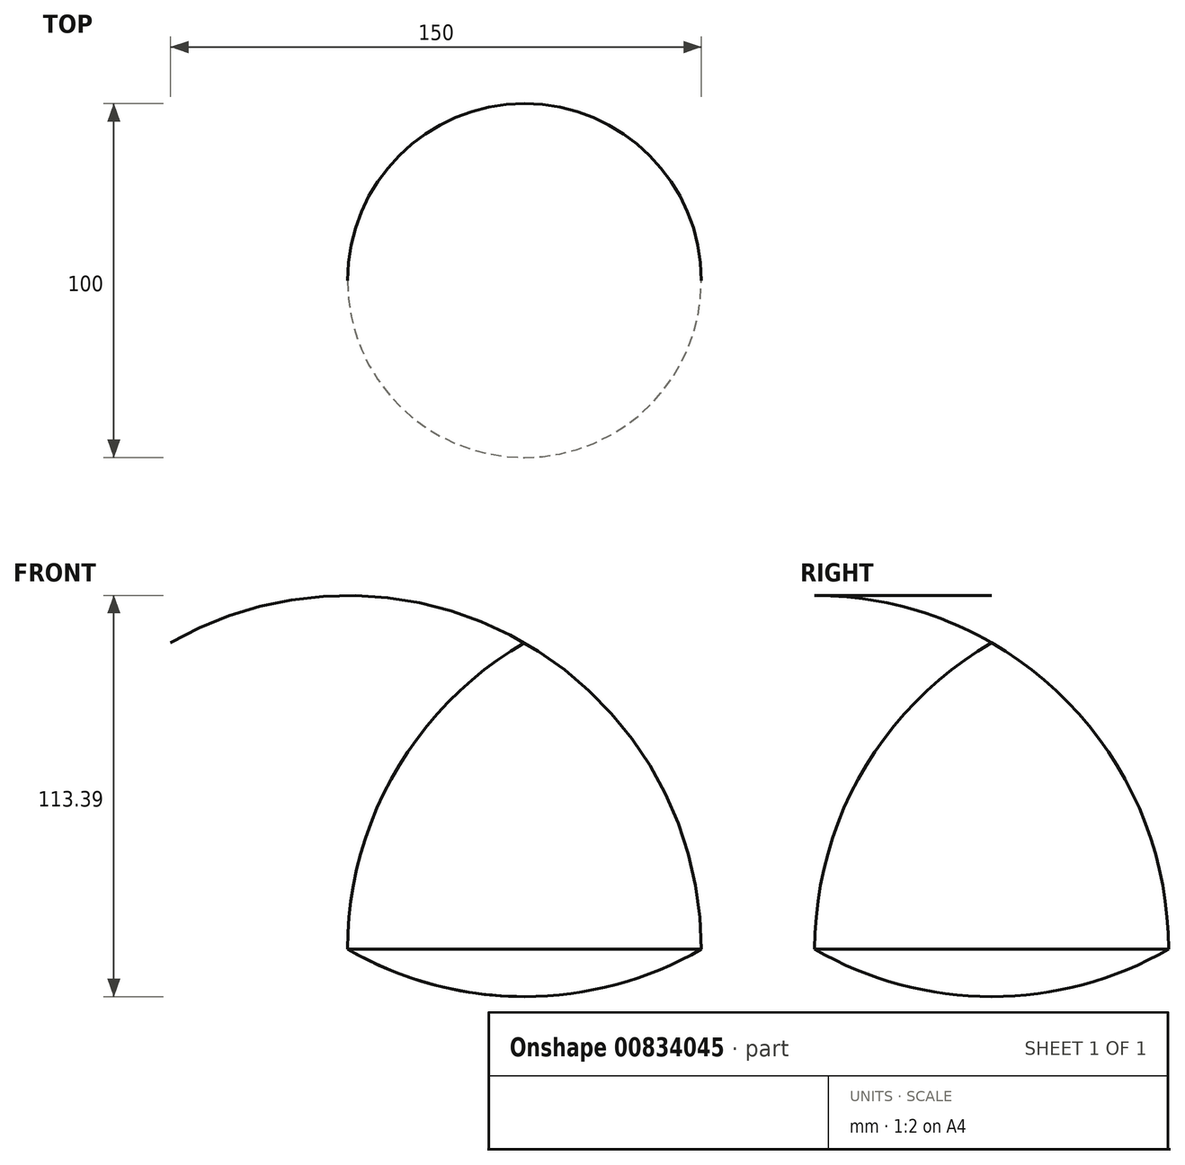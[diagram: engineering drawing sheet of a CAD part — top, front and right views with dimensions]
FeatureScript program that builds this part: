
annotation { "Feature Type Name" : "Feature", "Feature Type Description" : "" }
export const myFeature = defineFeature(function(context is Context, id is Id, definition is map)
    precondition{}
    {
        {
            var Q0;
            Q0=qCreatedBy(makeId("Front.planeOp"),FACE);
            var sketch = newSketch(context, id + "F0", { "sketchPlane" : qUnion([Q0])});
            skCircle(sketch, "E0.cCircle", {"center": v(0, 0) * mm, "radius": 28.87 * mm, "construction": true});
            skLineSegment(sketch, "E0.0", {"start": v(0, 57.74) * mm, "end": v(50, -28.87) * mm, "construction": true});
            skLineSegment(sketch, "E0.1", {"start": v(50, -28.87) * mm, "end": v(-50, -28.87) * mm, "construction": true});
            skLineSegment(sketch, "E0.2", {"start": v(-50, -28.87) * mm, "end": v(0, 57.74) * mm, "construction": true});
            skPoint(sketch, "E0.0.midPoint", {"position": v(25, 14.43) * mm});
            skArc(sketch, "E1", {"start": v(50, -28.87) * mm, "mid": v(36.6, 21.13) * mm, "end": v(0, 57.74) * mm});
            skArc(sketch, "E2", {"start": v(-50, -28.87) * mm, "mid": v(0, -42.26) * mm, "end": v(50, -28.87) * mm});
            skArc(sketch, "E3", {"start": v(0, 57.74) * mm, "mid": v(-36.6, 21.13) * mm, "end": v(-50, -28.87) * mm});
            skLineSegment(sketch, "E4", {"start": v(0, -42.26) * mm, "end": v(0, 57.74) * mm});
            skSolve(sketch);
        }
        {
            var Q0;
            {var subQ0=sQuery(id+"F0.wireOp",EDGE,"E3");Q0=makeQuery(id+"F0.imprint","IMPRINT",FACE,{"disambiguationData":[TD([[makeQuery(id+"F0.imprint","IMPRINT",EDGE,{"derivedFrom":subQ0}),1.0]])]});}
            var Q1;
            Q1=sQuery(id+"F0.wireOp",EDGE,"E4");
            revolve(context, id + "F1", {"surfaceOperationType" : NewSurfaceOperationType.NEW, "entities" : qUnion([Q0]), "axis" : qUnion([Q1]), "revolveType" : RevolveType.FULL});
        }
    });
